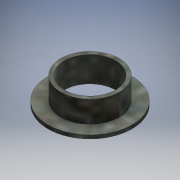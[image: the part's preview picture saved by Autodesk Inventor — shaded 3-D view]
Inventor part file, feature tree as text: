
AUTODESK INVENTOR PART (.ipt)
format: ipt  version: 2020.2 (Build 242310000, 310)  size: 119,808 bytes
history: native  units: mm
features: extrude x2, other x1, sketch x1
ambient origin geometry x8: Origin, YZ Plane, XZ Plane, XY Plane, X Axis, Y Axis, Z Axis, Center Point
bodies: Body1 (feature_tree)
feature tree (4):
  other  "ソリッド1"
  sketch  "スケッチ1"
  extrude  "押し出し1"  Depth=7.0mm
  extrude  "押し出し2"  Depth=8.0mm
